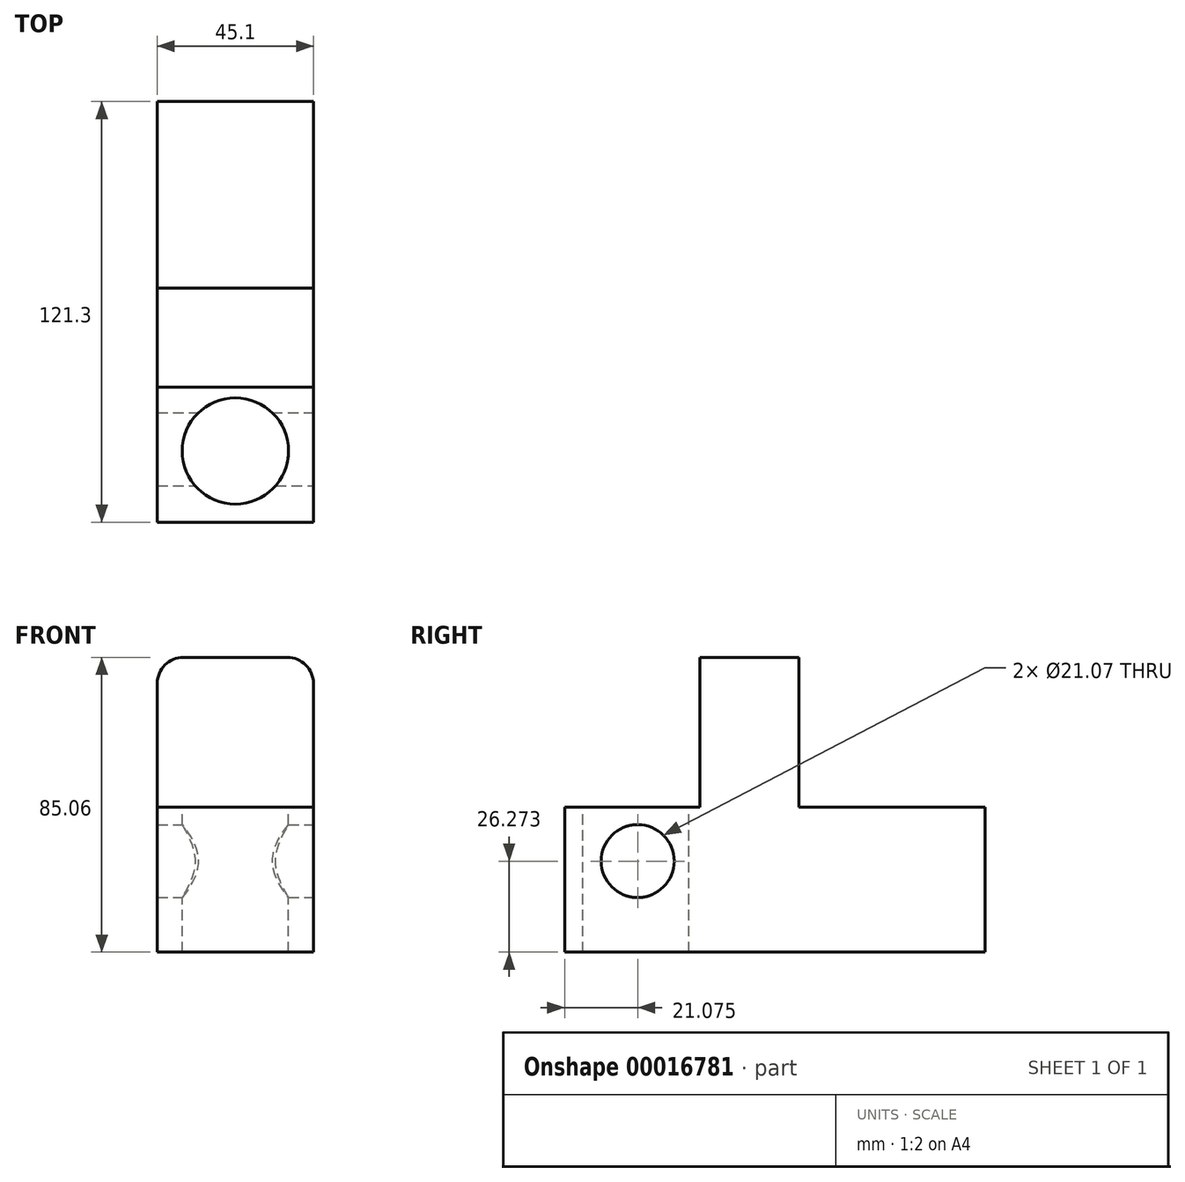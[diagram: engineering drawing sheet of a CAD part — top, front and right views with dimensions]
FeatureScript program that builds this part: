
annotation { "Feature Type Name" : "Feature", "Feature Type Description" : "" }
export const myFeature = defineFeature(function(context is Context, id is Id, definition is map)
    precondition{}
    {
        {
            var Q0;
            Q0=qCreatedBy(makeId("Top.planeOp"),FACE);
            var sketch = newSketch(context, id + "F0", { "sketchPlane" : qUnion([Q0])});
            skLineSegment(sketch, "E0.rect.bottom", {"start": v(-22.55, 22.55) * mm, "end": v(22.55, 22.55) * mm});
            skLineSegment(sketch, "E0.rect.top", {"start": v(-22.55, -22.55) * mm, "end": v(22.55, -22.55) * mm});
            skLineSegment(sketch, "E0.rect.left", {"start": v(-22.55, 22.55) * mm, "end": v(-22.55, -22.55) * mm});
            skLineSegment(sketch, "E0.rect.right", {"start": v(22.55, 22.55) * mm, "end": v(22.55, -22.55) * mm});
            skPoint(sketch, "E0.rect.middle", {"position": v(0, 0) * mm});
            skSolve(sketch);
        }
        {
            var Q0;
            Q0=makeQuery(id+"F0.imprint","IMPRINT",FACE,{"disambiguationData":[TD([[makeQuery(id+"F0.imprint","IMPRINT",EDGE,{"derivedFrom":sQuery(id+"F0.wireOp",EDGE,"E0.rect.bottom")}),-1.0]])]});
            extrude(context, id + "F1", {"entities" : qUnion([Q0]), "depth" : 41.88 * mm});
        }
        {
            var Q0;
            Q0=makeQuery(id+"F1.opExtrude","SWEPT_FACE",FACE,{"disambiguationData":[OSD([sQuery(id+"F0.wireOp",EDGE,"E0.rect.top")])]});
            extrude(context, id + "F2", {"entities" : qUnion([Q0]), "operationType" : NewBodyOperationType.ADD, "depth" : 50.8 * mm});
        }
        {
            var Q0;
            {var subQ0=sQuery(id+"F0.wireOp",EDGE,"E0.rect.top");Q0=makeQuery(id+"F2.boolean.opBoolean","MERGE",FACE,{"derivedFrom":[makeQuery(id+"F1.opExtrude","CAP_FACE",FACE,{"disambiguationData":[OSD([sQuery(id+"F0.wireOp",EDGE,"E0.rect.bottom"),subQ0,sQuery(id+"F0.wireOp",EDGE,"E0.rect.left"),sQuery(id+"F0.wireOp",EDGE,"E0.rect.right")])],"isStart":false}),makeQuery(id+"F2.opExtrude","SWEPT_FACE",FACE,{"disambiguationData":[OSD([subQ0]),TDD([makeQuery(id+"F1.opExtrude","CAP_EDGE",EDGE,{"disambiguationData":[OSD([subQ0])],"isStart":false})])]})]});}
            var sketch = newSketch(context, id + "F3", { "sketchPlane" : qUnion([Q0])});
            skLineSegment(sketch, "E1", {"start": v(-22.55, -5.8) * mm, "end": v(22.55, -5.8) * mm});
            skLineSegment(sketch, "E2", {"start": v(-22.55, -34.37) * mm, "end": v(22.55, -34.37) * mm});
            skSolve(sketch);
        }
        {
            var Q0;
            {var subQ4=sQuery(id+"F3.wireOp",EDGE,"E1");Q0=makeQuery(id+"F3.imprint","IMPRINT",FACE,{"disambiguationData":[TD([[makeQuery(id+"F3.imprint","IMPRINT",EDGE,{"derivedFrom":subQ4}),-1.0]])]});}
            extrude(context, id + "F4", {"entities" : qUnion([Q0]), "operationType" : NewBodyOperationType.ADD, "depth" : 12.7 * mm});
        }
        {
            var Q0;
            {var subQ0=sQuery(id+"F0.wireOp",EDGE,"E0.rect.right");var subQ1=sQuery(id+"F0.wireOp",EDGE,"E0.rect.top");Q0=makeQuery(id+"F4.boolean.opBoolean","MERGE",FACE,{"derivedFrom":[makeQuery(id+"F2.boolean.opBoolean","MERGE",FACE,{"derivedFrom":[makeQuery(id+"F1.opExtrude","SWEPT_FACE",FACE,{"disambiguationData":[OSD([subQ0])]}),makeQuery(id+"F2.opExtrude","SWEPT_FACE",FACE,{"disambiguationData":[OSD([subQ1,subQ0])]})]}),makeQuery(id+"F4.opExtrude","SWEPT_FACE",FACE,{"disambiguationData":[OSD([subQ1,subQ0])]})]});}
            var sketch = newSketch(context, id + "F5", { "sketchPlane" : qUnion([Q0])});
            skCircle(sketch, "E3", {"center": v(-52.27, 26.27) * mm, "radius": 10.54 * mm});
            skSolve(sketch);
        }
        {
            var Q0;
            Q0=makeQuery(id+"F5.imprint","IMPRINT",FACE,{"disambiguationData":[TD([[makeQuery(id+"F5.imprint","IMPRINT",EDGE,{"derivedFrom":sQuery(id+"F5.wireOp",EDGE,"E3")}),1.0]])]});
            extrude(context, id + "F6", {"entities" : qUnion([Q0]), "operationType" : NewBodyOperationType.REMOVE, "oppositeDirection" : true, "depth" : 46.77 * mm});
        }
        {
            var Q0;
            {var subQ0=sQuery(id+"F0.wireOp",EDGE,"E0.rect.top");var subQ1=sQuery(id+"F0.wireOp",EDGE,"E0.rect.left");var subQ2=sQuery(id+"F0.wireOp",EDGE,"E0.rect.right");Q0=makeQuery(id+"F4.boolean.opBoolean","SPLIT",FACE,{"disambiguationData":[TD([makeQuery(id+"F2.opExtrude","CAP_FACE",FACE,{"disambiguationData":[OSD([subQ0])],"isStart":false})])],"derivedFrom":makeQuery(id+"F2.boolean.opBoolean","MERGE",FACE,{"derivedFrom":[makeQuery(id+"F1.opExtrude","CAP_FACE",FACE,{"disambiguationData":[OSD([sQuery(id+"F0.wireOp",EDGE,"E0.rect.bottom"),subQ0,subQ1,subQ2])],"isStart":false}),makeQuery(id+"F2.opExtrude","SWEPT_FACE",FACE,{"disambiguationData":[OSD([subQ0]),TDD([makeQuery(id+"F1.opExtrude","CAP_EDGE",EDGE,{"disambiguationData":[OSD([subQ0])],"isStart":false})])]})]})});}
            var sketch = newSketch(context, id + "F7", { "sketchPlane" : qUnion([Q0])});
            skCircle(sketch, "E4", {"center": v(0, -52.83) * mm, "radius": 15.34 * mm});
            skSolve(sketch);
        }
        {
            var Q0;
            Q0=makeQuery(id+"F7.imprint","IMPRINT",FACE,{"disambiguationData":[TD([[makeQuery(id+"F7.imprint","IMPRINT",EDGE,{"derivedFrom":sQuery(id+"F7.wireOp",EDGE,"E4")}),1.0]])]});
            extrude(context, id + "F8", {"entities" : qUnion([Q0]), "operationType" : NewBodyOperationType.REMOVE, "oppositeDirection" : true, "depth" : 43.63 * mm});
        }
        {
            var Q0;
            Q0=makeQuery(id+"F1.opExtrude","SWEPT_FACE",FACE,{"disambiguationData":[OSD([sQuery(id+"F0.wireOp",EDGE,"E0.rect.bottom")])]});
            extrude(context, id + "F9", {"entities" : qUnion([Q0]), "operationType" : NewBodyOperationType.ADD, "depth" : 25.4 * mm});
        }
        {
            var Q0;
            Q0=makeQuery(id+"F4.opExtrude","CAP_FACE",FACE,{"disambiguationData":[OSD([sQuery(id+"F0.wireOp",EDGE,"E0.rect.top"),sQuery(id+"F0.wireOp",EDGE,"E0.rect.left"),sQuery(id+"F0.wireOp",EDGE,"E0.rect.right"),sQuery(id+"F3.wireOp",EDGE,"E1"),sQuery(id+"F3.wireOp",EDGE,"E2")])],"isStart":false});
            extrude(context, id + "F10", {"entities" : qUnion([Q0]), "operationType" : NewBodyOperationType.ADD, "depth" : 30.48 * mm});
        }
        {
            var Q0;
            Q0=makeQuery(id+"F10.opExtrude","CAP_EDGE",EDGE,{"disambiguationData":[OSD([sQuery(id+"F0.wireOp",EDGE,"E0.rect.top"),sQuery(id+"F0.wireOp",EDGE,"E0.rect.left")])],"isStart":false});
            var Q1;
            Q1=makeQuery(id+"F10.opExtrude","CAP_EDGE",EDGE,{"disambiguationData":[OSD([sQuery(id+"F0.wireOp",EDGE,"E0.rect.top"),sQuery(id+"F0.wireOp",EDGE,"E0.rect.right")])],"isStart":false});
            fillet(context, id + "F11", {"entities" : qUnion([Q0, Q1]), "tangentPropagation" : true, "radius" : 7.62 * mm, "defaultsChanged" : true, "vertexSettings" : [], "allowEdgeOverflow" : false});
        }
    });
